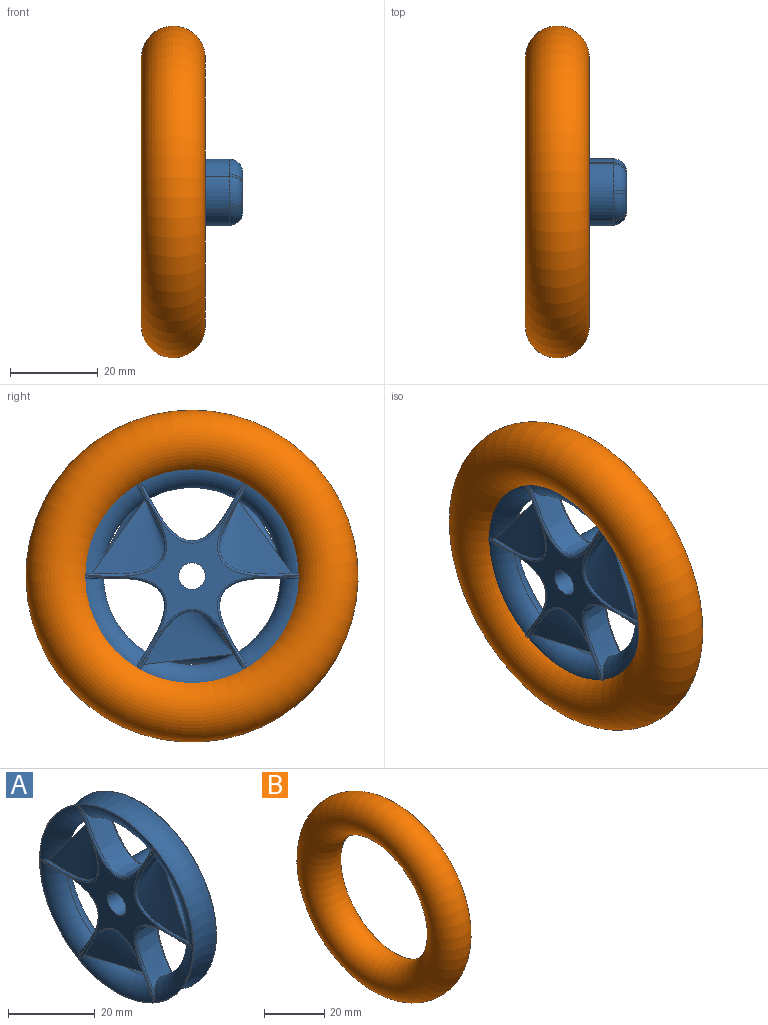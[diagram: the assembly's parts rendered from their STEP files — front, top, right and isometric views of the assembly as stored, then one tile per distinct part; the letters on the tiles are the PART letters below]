
ASSEMBLY  parts=2 mates=1
PART A: 90 faces, bbox 20.7x64.9x61.8 mm
  f0: plane 50.18x50.18mm, normal (1,0,0), area 24.9mm2, adj f9,f30,f32,f34,f36,f38,f40,f48
  f1: plane 9.25x7.36mm, normal (1,0,0), area 13.2mm2, adj f17,f68,f70
  f2: plane 8.66x7.01mm, normal (1,0,0), area 13.2mm2, adj f19,f58,f60
  f3: plane 9.25x7.37mm, normal (1,0,0), area 13.2mm2, adj f21,f48,f50
  f4: plane 9.25x7.36mm, normal (1,0,0), area 13.2mm2, adj f11,f55,f57
  f5: plane 8.66x7.01mm, normal (1,0,0), area 13.2mm2, adj f13,f65,f67
  f6: plane 50.18x50.18mm, normal (-1,0,0), area 24.9mm2, adj f9,f31,f33,f35,f37,f39,f41,f42
  f7: plane 9.25x7.36mm, normal (1,0,0), area 13.2mm2, adj f15,f75,f77
  f8: plane 30.64x26.53mm, normal (-1,0,0), area 228.2mm2, adj f10,f42,f43,f44,f45,f46,f47
  f9: torus R=31mm, axis (1,0,0), area 1211.8mm2, adj f0,f6
  f10: cylinder r=3.02mm len=19.5mm, axis (1,0,0), area 370.6mm2, adj f8,f23
  f11: cylinder r=7.53mm len=9mm, axis (-1,0,0), area 65.5mm2, adj f4,f12,f22,f54,f59,f86
  f12: cylinder r=5.11mm len=9mm, axis (-1,0,0), area 5.4mm2, adj f11,f13,f61,f84
  f13: cylinder r=7.53mm len=9mm, axis (-1,0,0), area 65.5mm2, adj f5,f12,f14,f64,f69,f82
  f14: cylinder r=5.11mm len=9mm, axis (-1,0,0), area 5.4mm2, adj f13,f15,f71,f80
  f15: cylinder r=7.53mm len=9mm, axis (-1,0,0), area 65.5mm2, adj f7,f14,f16,f74,f76,f78
  f16: cylinder r=5.11mm len=9mm, axis (-1,0,0), area 5.4mm2, adj f15,f17,f73,f79
  f17: cylinder r=7.53mm len=9mm, axis (-1,0,0), area 65.5mm2, adj f1,f16,f18,f66,f72,f81
  f18: cylinder r=5.11mm len=9mm, axis (-1,0,0), area 5.4mm2, adj f17,f19,f63,f83
  f19: cylinder r=7.53mm len=9mm, axis (-1,0,0), area 65.5mm2, adj f2,f18,f20,f56,f62,f85
  f20: cylinder r=5.11mm len=9mm, axis (-1,0,0), area 5.4mm2, adj f19,f21,f53,f87
  f21: cylinder r=7.53mm len=9mm, axis (-1,0,0), area 65.5mm2, adj f3,f20,f22,f49,f52,f89
  f22: cylinder r=5.11mm len=9mm, axis (-1,0,0), area 5.4mm2, adj f11,f21,f51,f88
  f23: plane 9.05x9.03mm, normal (1,0,0), area 35.6mm2, adj f10,f78,f79,f80,f81,f82,f83,f84
  f24: extruded ~18.98x16.52mm, area 197.4mm2, adj f40,f41,f44,f67,f69,f71,f74,f75
  f25: extruded ~21.67x12.05mm, area 197.4mm2, adj f38,f39,f46,f70,f72,f73,f76,f77
  f26: extruded ~21.67x12.05mm, area 197.4mm2, adj f36,f37,f43,f48,f49,f51,f54,f55
  f27: extruded ~18.98x16.52mm, area 197.4mm2, adj f34,f35,f42,f57,f59,f61,f64,f65
  f28: extruded ~18.98x16.52mm, area 197.4mm2, adj f32,f33,f45,f50,f52,f53,f56,f58
  f29: extruded ~18.98x16.52mm, area 197.4mm2, adj f30,f31,f47,f60,f62,f63,f66,f68
  f30: torus R=24.98mm, axis (-1,0,0), area 145.5mm2, adj f0,f29,f31,f60,f68
  f31: torus R=24.98mm, axis (1,0,0), area 145.5mm2, adj f6,f29,f30,f47
  f32: torus R=24.98mm, axis (-1,0,0), area 145.5mm2, adj f0,f28,f33,f50,f58
  f33: torus R=24.98mm, axis (1,0,0), area 145.5mm2, adj f6,f28,f32,f45
  f34: torus R=24.98mm, axis (-1,0,0), area 145.5mm2, adj f0,f27,f35,f57,f65
  f35: torus R=24.98mm, axis (1,0,0), area 145.5mm2, adj f6,f27,f34,f42
  f36: torus R=24.98mm, axis (-1,0,0), area 145.5mm2, adj f0,f26,f37,f48,f55
  f37: torus R=24.98mm, axis (1,0,0), area 145.5mm2, adj f6,f26,f36,f43
  f38: torus R=24.98mm, axis (-1,0,0), area 145.5mm2, adj f0,f25,f39,f70,f77
  f39: torus R=24.98mm, axis (1,0,0), area 145.5mm2, adj f6,f25,f38,f46
  f40: torus R=24.98mm, axis (-1,0,0), area 145.5mm2, adj f0,f24,f41,f67,f75
  f41: torus R=24.98mm, axis (1,0,0), area 145.5mm2, adj f6,f24,f40,f44
  f42: bspline ~25.26x22.7mm, area 28.6mm2, adj f6,f8,f27,f35,f43,f44
  f43: bspline ~30.63x22.54mm, area 28.6mm2, adj f6,f8,f26,f37,f42,f45
  f44: bspline ~29.16x23.61mm, area 28.6mm2, adj f6,f8,f24,f41,f42,f46
  f45: bspline ~24.49x23.61mm, area 28.6mm2, adj f6,f8,f28,f33,f43,f47
  f46: bspline ~28.11x18.4mm, area 28.6mm2, adj f6,f8,f25,f39,f44,f47
  f47: bspline ~28.24x25.26mm, area 28.6mm2, adj f6,f8,f29,f31,f45,f46
  f48: bspline ~18.4x14.4mm, area 14.1mm2, adj f0,f3,f26,f36,f49,f50
  f49: bspline ~0.55x0.54mm, area 0mm2, adj f21,f26,f48,f51
  f50: bspline ~20.98x9.26mm, area 14.1mm2, adj f0,f3,f28,f32,f48,f52
  f51: bspline ~1.17x0.55mm, area 0.4mm2, adj f22,f26,f49,f54
  f52: bspline ~1.01x0.91mm, area 0mm2, adj f21,f28,f50,f53
  f53: bspline ~1.22x0.97mm, area 0.4mm2, adj f20,f28,f52,f56
  f54: bspline ~0.58x0.53mm, area 0mm2, adj f11,f26,f51,f55
  f55: bspline ~22.54x16.74mm, area 14.1mm2, adj f0,f4,f26,f36,f54,f57
  f56: bspline ~1.03x0.89mm, area 0mm2, adj f19,f28,f53,f58
  f57: bspline ~21.61x9.76mm, area 14.1mm2, adj f0,f4,f27,f34,f55,f59
  f58: bspline ~22.97x4.23mm, area 14.1mm2, adj f0,f2,f28,f32,f56,f60
  f59: bspline ~1.02x0.89mm, area 0mm2, adj f11,f27,f57,f61
  f60: bspline ~27.69x4.36mm, area 14.1mm2, adj f0,f2,f29,f30,f58,f62
  f61: bspline ~1.22x1.01mm, area 0.4mm2, adj f12,f27,f59,f64
  f62: bspline ~0.75x0.71mm, area 0mm2, adj f19,f29,f60,f63
  f63: bspline ~1.22x1.01mm, area 0.4mm2, adj f18,f29,f62,f66
  f64: bspline ~1.05x0.89mm, area 0mm2, adj f13,f27,f61,f65
  f65: bspline ~22.13x4.36mm, area 14.1mm2, adj f0,f5,f27,f34,f64,f67
  f66: bspline ~0.68x0.61mm, area 0mm2, adj f17,f29,f63,f68
  f67: bspline ~22.94x4.19mm, area 14.1mm2, adj f0,f5,f24,f40,f65,f69
  f68: bspline ~21.56x9.77mm, area 14.1mm2, adj f0,f1,f29,f30,f66,f70
  f69: bspline ~0.67x0.65mm, area 0mm2, adj f13,f24,f67,f71
  f70: bspline ~17.58x14.21mm, area 14.1mm2, adj f0,f1,f25,f38,f68,f72
  f71: bspline ~1.22x0.97mm, area 0.4mm2, adj f14,f24,f69,f74
  f72: bspline ~0.92x0.6mm, area 0mm2, adj f17,f25,f70,f73
  f73: bspline ~1.17x0.55mm, area 0.4mm2, adj f16,f25,f72,f76
  f74: bspline ~0.73x0.71mm, area 0mm2, adj f15,f24,f71,f75
  f75: bspline ~25.65x12.3mm, area 14.1mm2, adj f0,f7,f24,f40,f74,f77
  f76: bspline ~0.93x0.55mm, area 0mm2, adj f15,f25,f73,f77
  f77: bspline ~18.4x14.46mm, area 14.1mm2, adj f0,f7,f25,f38,f75,f76
  f78: torus R=4.53mm, axis (1,0,0), area 28.6mm2, adj f15,f23,f79,f80
  f79: torus R=8.11mm, axis (1,0,0), area 2.7mm2, adj f16,f23,f78,f81
  f80: torus R=8.11mm, axis (1,0,0), area 2.7mm2, adj f14,f23,f78,f82
  f81: torus R=4.53mm, axis (1,0,0), area 28.6mm2, adj f17,f23,f79,f83
  f82: torus R=4.53mm, axis (1,0,0), area 28.6mm2, adj f13,f23,f80,f84
  f83: torus R=8.11mm, axis (1,0,0), area 2.7mm2, adj f18,f23,f81,f85
  f84: torus R=8.11mm, axis (1,0,0), area 2.7mm2, adj f12,f23,f82,f86
  f85: torus R=4.53mm, axis (1,0,0), area 28.6mm2, adj f19,f23,f83,f87
  f86: torus R=4.53mm, axis (1,0,0), area 28.6mm2, adj f11,f23,f84,f88
  f87: torus R=8.11mm, axis (1,0,0), area 2.7mm2, adj f20,f23,f85,f89
  f88: torus R=8.11mm, axis (1,0,0), area 2.7mm2, adj f22,f23,f86,f89
  f89: torus R=4.53mm, axis (1,0,0), area 28.6mm2, adj f21,f23,f87,f88
PART B: 1 faces, bbox 14.5x81.7x81.7 mm
  f0: torus R=30.5mm, axis (-1,0,0), area 8729.7mm2
PLACE A t=(-26.11,-0.47,21.9)mm
PLACE B t=(-26.11,-0.47,21.9)mm
MATE fastened A.f9 <-> B.f0  axis (1,0,0) through (-26.11,-0.47,21.9)mm
